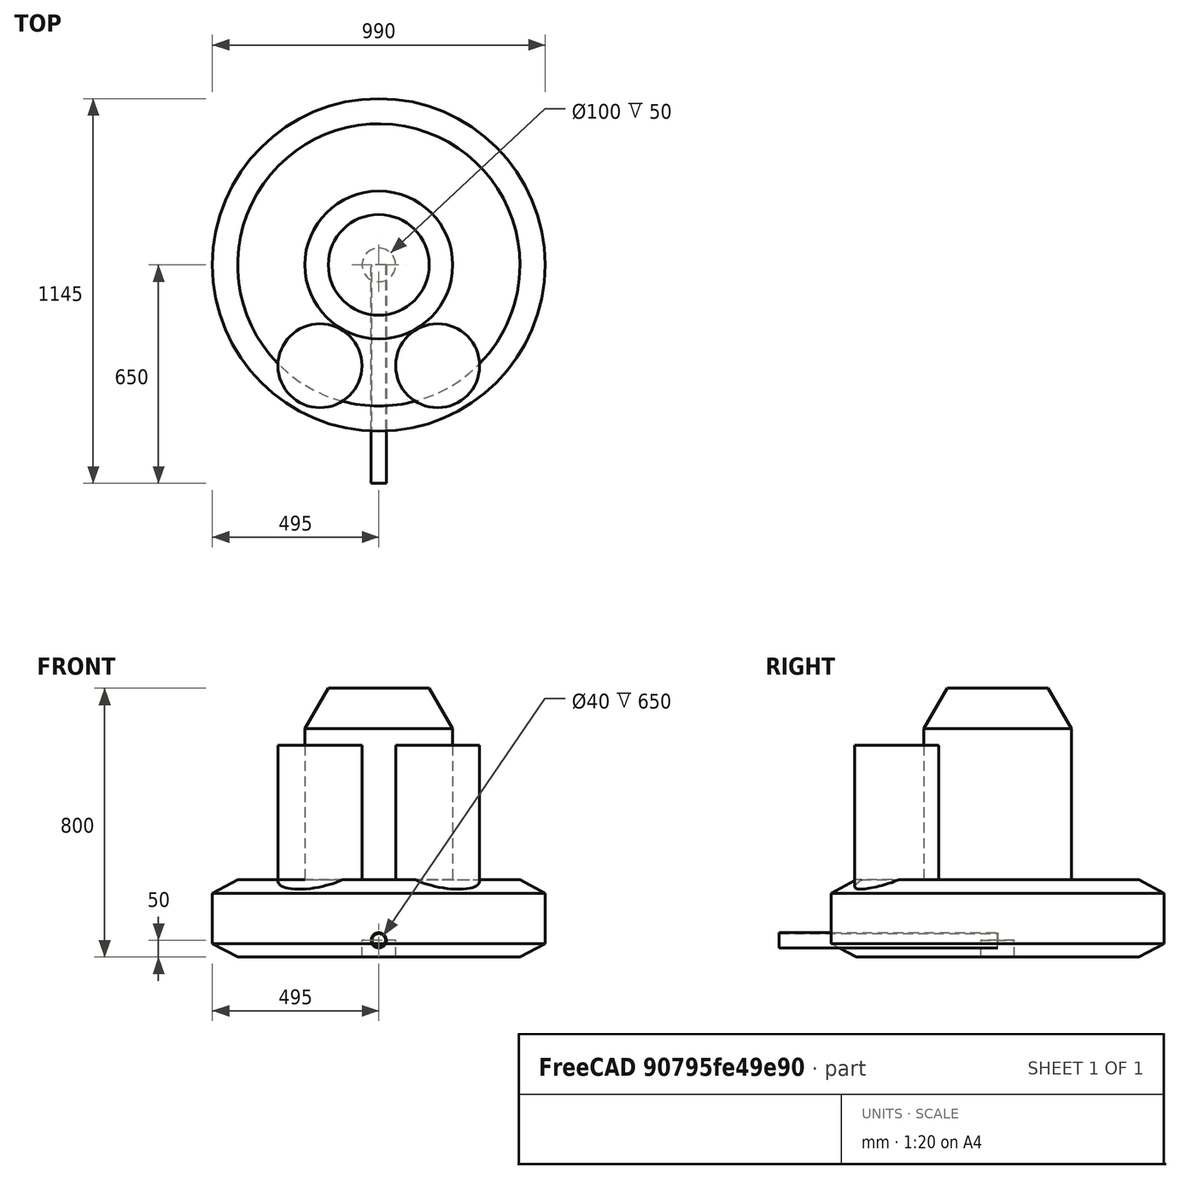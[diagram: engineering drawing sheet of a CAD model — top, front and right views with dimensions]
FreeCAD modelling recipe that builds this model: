
FCSTD DOCUMENT  (FreeCAD 1.0R39285 (Git))
Label: pipe2.5
License: All rights reserved
LicenseURL: https://en.wikipedia.org/wiki/All_rights_reserved
objects: Sketcher::SketchObject×1, PartDesign::Pad×1, PartDesign::Body×1, Part::FeaturePython×1
note: 7 computed .brp shape members not serialized (recipe doc carries the construction recipe); baked Part::Feature solids carry a one-line shape summary decoded from their .brp

FEATURE [Sketcher::SketchObject] Sketch
  ArcFitTolerance = 1e-06
  AttachmentSupport = -> [XZ_Plane]
  FullyConstrained = true
  MakeInternals = false
  MapMode = 5
  Placement = pos=(0,0,0) rot=(1,0,0;1.5708rad)
  sketch-geometry (2):
    g0: Circle CenterX=0 CenterY=0 CenterZ=0 NormalX=0 NormalY=0 NormalZ=1 AngleXU=0 Radius=20
    g1: Circle CenterX=0 CenterY=0 CenterZ=0 NormalX=0 NormalY=0 NormalZ=1 AngleXU=0 Radius=22.5
  constraints (4):
    c: Diameter(g0) = 40
    c: Coincident(g0,g-1)
    c: Diameter(g1) = 45
    c: Coincident(g1,g0)
FEATURE [PartDesign::Pad] Pad
  Direction = (0,-1,2e-16)
  Length = 650
  Length2 = 10
  Placement = pos=(0,0,0) rot=(1,0,0;1.5708rad)
  Profile = -> Sketch
  ReferenceAxis = -> Sketch [N_Axis]
  Refine = true
  Suppressed = false
  Type = 0
FEATURE [PartDesign::Body] Body
  AllowCompound = false
  Group = -> [Sketch,Pad]
  Origin = -> Origin
  Tip = -> Pad
FEATURE [Part::FeaturePython] b_motor_001_  label="motor_001"  # a2plus imported part (geometry in sourceFile) (typed FeaturePython)
  a2p_Version = 0.4.68
  fixedPosition = true
  objectType = a2pPart
  sourceFile = .\motor.FCStd
  subassemblyImport = false
  timeLastImport = 1.75293e+09
  updateColors = true
